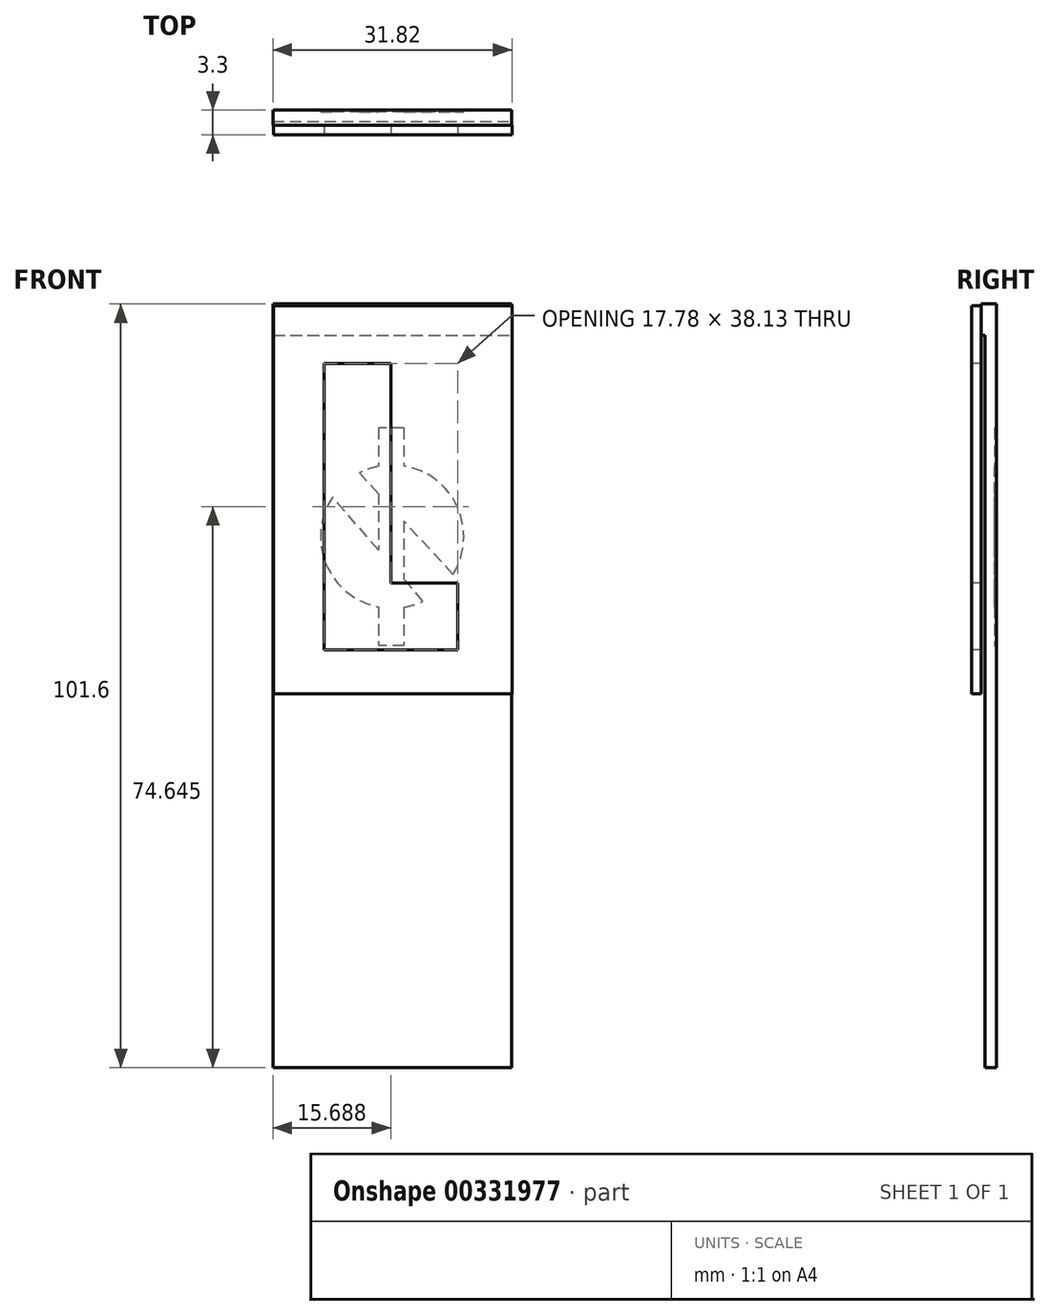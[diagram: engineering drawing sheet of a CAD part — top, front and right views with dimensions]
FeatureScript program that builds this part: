
annotation { "Feature Type Name" : "Feature", "Feature Type Description" : "" }
export const myFeature = defineFeature(function(context is Context, id is Id, definition is map)
    precondition{}
    {
        {
            var Q0;
            Q0=qCreatedBy(makeId("Front.planeOp"),FACE);
            var sketch = newSketch(context, id + "F0", { "sketchPlane" : qUnion([Q0])});
            skLineSegment(sketch, "E0.bottom", {"start": v(-28.9, 62.6) * mm, "end": v(2.85, 62.6) * mm});
            skLineSegment(sketch, "E0.top", {"start": v(-28.9, -39) * mm, "end": v(2.85, -39) * mm});
            skLineSegment(sketch, "E0.left", {"start": v(-28.9, 62.6) * mm, "end": v(-28.9, -39) * mm});
            skLineSegment(sketch, "E0.right", {"start": v(2.85, 62.6) * mm, "end": v(2.85, -39) * mm});
            skSolve(sketch);
        }
        {
            var Q0;
            Q0=makeQuery(id+"F0.imprint","IMPRINT",FACE,{"disambiguationData":[TD([[makeQuery(id+"F0.imprint","IMPRINT",EDGE,{"derivedFrom":sQuery(id+"F0.wireOp",EDGE,"E0.bottom")}),-1.0]])]});
            extrude(context, id + "F1", {"entities" : qUnion([Q0]), "depth" : 1.52 * mm});
        }
        {
            var Q0;
            Q0=makeQuery(id+"F1.opExtrude","CAP_FACE",FACE,{"disambiguationData":[OSD([sQuery(id+"F0.wireOp",EDGE,"E0.bottom"),sQuery(id+"F0.wireOp",EDGE,"E0.top"),sQuery(id+"F0.wireOp",EDGE,"E0.left"),sQuery(id+"F0.wireOp",EDGE,"E0.right")])],"isStart":false});
            var sketch = newSketch(context, id + "F2", { "sketchPlane" : qUnion([Q0])});
            skLineSegment(sketch, "E1.bottom", {"start": v(-28.9, 62.6) * mm, "end": v(2.85, 62.6) * mm});
            skLineSegment(sketch, "E1.top", {"start": v(-28.9, 58.42) * mm, "end": v(2.85, 58.42) * mm});
            skLineSegment(sketch, "E1.left", {"start": v(-28.9, 62.6) * mm, "end": v(-28.9, 58.42) * mm});
            skLineSegment(sketch, "E1.right", {"start": v(2.85, 62.6) * mm, "end": v(2.85, 58.42) * mm});
            skSolve(sketch);
        }
        {
            var Q0;
            Q0=makeQuery(id+"F2.imprint","IMPRINT",FACE,{"disambiguationData":[TD([[makeQuery(id+"F2.imprint","IMPRINT",EDGE,{"derivedFrom":sQuery(id+"F2.wireOp",EDGE,"E1.bottom")}),-1.0]])]});
            extrude(context, id + "F3", {"entities" : qUnion([Q0]), "operationType" : NewBodyOperationType.ADD, "depth" : 0.5 * mm});
        }
        {
            var Q0;
            Q0=makeQuery(id+"F3.opExtrude","CAP_FACE",FACE,{"disambiguationData":[OSD([sQuery(id+"F2.wireOp",EDGE,"E1.bottom"),sQuery(id+"F2.wireOp",EDGE,"E1.top"),sQuery(id+"F2.wireOp",EDGE,"E1.left"),sQuery(id+"F2.wireOp",EDGE,"E1.right")])],"isStart":false});
            cPlane(context, id + "F4", {"entities" : qUnion([Q0]), "cplaneType" : CPlaneType.OFFSET, "offset" : 0 * mm, "width" : 152.4 * mm, "height" : 152.4 * mm});
        }
        {
            var Q0;
            Q0=qCreatedBy(id+"F4.planeOp",FACE);
            var sketch = newSketch(context, id + "F5", { "sketchPlane" : qUnion([Q0])});
            skLineSegment(sketch, "E2.bottom", {"start": v(-28.83, 62.35) * mm, "end": v(2.92, 62.35) * mm});
            skLineSegment(sketch, "E2.top", {"start": v(-28.83, 10.75) * mm, "end": v(2.92, 10.75) * mm});
            skLineSegment(sketch, "E2.left", {"start": v(-28.83, 62.35) * mm, "end": v(-28.83, 10.75) * mm});
            skLineSegment(sketch, "E2.right", {"start": v(2.92, 62.35) * mm, "end": v(2.92, 10.75) * mm});
            skSolve(sketch);
        }
        {
            var Q0;
            Q0=makeQuery(id+"F5.imprint","IMPRINT",FACE,{"disambiguationData":[TD([[makeQuery(id+"F5.imprint","IMPRINT",EDGE,{"derivedFrom":sQuery(id+"F5.wireOp",EDGE,"E2.bottom")}),-1.0]])]});
            extrude(context, id + "F6", {"entities" : qUnion([Q0]), "operationType" : NewBodyOperationType.ADD, "depth" : 1.27 * mm});
        }
        {
            var Q0;
            Q0=makeQuery(id+"F6.opExtrude","CAP_FACE",FACE,{"disambiguationData":[OSD([sQuery(id+"F5.wireOp",EDGE,"E2.bottom"),sQuery(id+"F5.wireOp",EDGE,"E2.top"),sQuery(id+"F5.wireOp",EDGE,"E2.left"),sQuery(id+"F5.wireOp",EDGE,"E2.right")])],"isStart":false});
            var sketch = newSketch(context, id + "F7", { "sketchPlane" : qUnion([Q0])});
            skPoint(sketch, "E3.3.internal.snap0", {"position": v(-12.95, 62.35) * mm});
            skLineSegment(sketch, "E4", {"start": v(-22.1, 54.71) * mm, "end": v(-22.1, 16.58) * mm});
            skLineSegment(sketch, "E5", {"start": v(-22.1, 16.58) * mm, "end": v(-4.32, 16.58) * mm});
            skLineSegment(sketch, "E6", {"start": v(-4.32, 16.58) * mm, "end": v(-4.32, 25.47) * mm});
            skLineSegment(sketch, "E7", {"start": v(-4.32, 25.47) * mm, "end": v(-13.21, 25.47) * mm});
            skPoint(sketch, "E7.endSnap0", {"position": v(-13.21, 16.58) * mm});
            skLineSegment(sketch, "E8", {"start": v(-13.21, 25.47) * mm, "end": v(-13.21, 54.71) * mm});
            skLineSegment(sketch, "E9", {"start": v(-22.1, 54.71) * mm, "end": v(-13.21, 54.71) * mm});
            skSolve(sketch);
        }
        {
            var Q0;
            Q0=makeQuery(id+"F7.imprint","IMPRINT",FACE,{"disambiguationData":[TD([[makeQuery(id+"F7.imprint","IMPRINT",EDGE,{"derivedFrom":sQuery(id+"F7.wireOp",EDGE,"E4")}),1.0]])]});
            extrude(context, id + "F8", {"entities" : qUnion([Q0]), "operationType" : NewBodyOperationType.REMOVE, "oppositeDirection" : true, "depth" : 1.27 * mm});
        }
        {
            var Q0;
            Q0=makeQuery(id+"F1.opExtrude","CAP_FACE",FACE,{"disambiguationData":[OSD([sQuery(id+"F0.wireOp",EDGE,"E0.bottom"),sQuery(id+"F0.wireOp",EDGE,"E0.top"),sQuery(id+"F0.wireOp",EDGE,"E0.left"),sQuery(id+"F0.wireOp",EDGE,"E0.right")])],"isStart":true});
            var sketch = newSketch(context, id + "F9", { "sketchPlane" : qUnion([Q0])});
            skCircle(sketch, "E10", {"center": v(13.03, 31.66) * mm, "radius": 12.7 * mm});
            skPoint(sketch, "E10.centerSnap0", {"position": v(13.03, 62.6) * mm});
            skCircle(sketch, "E11", {"center": v(13.03, 31.66) * mm, "radius": 9.53 * mm});
            skLineSegment(sketch, "E12", {"start": v(4.94, 26.64) * mm, "end": v(17.4, 40.13) * mm});
            skLineSegment(sketch, "E13", {"start": v(8.92, 23.06) * mm, "end": v(20.97, 36.92) * mm});
            skSolve(sketch);
        }
        {
            var Q0;
            {var subQ0=sQuery(id+"F9.wireOp",EDGE,"E12");Q0=makeQuery(id+"F9.imprint","IMPRINT",FACE,{"disambiguationData":[TD([[makeQuery(id+"F9.imprint","IMPRINT",EDGE,{"derivedFrom":subQ0}),1.0]])]});}
            var Q1;
            {var subQ0=sQuery(id+"F9.wireOp",EDGE,"E13");Q1=makeQuery(id+"F9.imprint","IMPRINT",FACE,{"disambiguationData":[TD([[makeQuery(id+"F9.imprint","IMPRINT",EDGE,{"derivedFrom":subQ0}),-1.0]])]});}
            extrude(context, id + "F10", {"entities" : qUnion([Q0, Q1]), "operationType" : NewBodyOperationType.REMOVE, "depth" : -0.25 * mm});
        }
        {
            var Q0;
            Q0=makeQuery(id+"F1.opExtrude","CAP_FACE",FACE,{"disambiguationData":[OSD([sQuery(id+"F0.wireOp",EDGE,"E0.bottom"),sQuery(id+"F0.wireOp",EDGE,"E0.top"),sQuery(id+"F0.wireOp",EDGE,"E0.left"),sQuery(id+"F0.wireOp",EDGE,"E0.right")])],"isStart":true});
            var sketch = newSketch(context, id + "F11", { "sketchPlane" : qUnion([Q0])});
            skLineSegment(sketch, "E14.bottom", {"start": v(11.46, 46.09) * mm, "end": v(14.85, 46.09) * mm});
            skLineSegment(sketch, "E14.top", {"start": v(11.46, 17.18) * mm, "end": v(14.85, 17.18) * mm});
            skLineSegment(sketch, "E14.left", {"start": v(11.46, 46.09) * mm, "end": v(11.46, 17.18) * mm});
            skLineSegment(sketch, "E14.right", {"start": v(14.85, 46.09) * mm, "end": v(14.85, 17.18) * mm});
            skPoint(sketch, "E15", {"position": v(14.85, 41) * mm});
            skPoint(sketch, "E16", {"position": v(11.46, 22.26) * mm});
            skSolve(sketch);
        }
        {
            var Q0;
            {var subQ0=sQuery(id+"F11.wireOp",EDGE,"E14.bottom");Q0=makeQuery(id+"F11.imprint","IMPRINT",FACE,{"disambiguationData":[TD([[makeQuery(id+"F11.imprint","IMPRINT",EDGE,{"derivedFrom":subQ0}),-1.0]])]});}
            var Q1;
            {var subQ0=sQuery(id+"F11.wireOp",EDGE,"E14.left");var subQ1=makeQuery(id+"F10.boolean.opBoolean","COPY",EDGE,{"derivedFrom":makeQuery(id+"F10.opExtrude","CAP_EDGE",EDGE,{"disambiguationData":[OSD([sQuery(id+"F9.wireOp",EDGE,"E12")])],"isStart":true})});var subQ2=makeQuery(id+"F11.imprint","INTERSECT",VERTEX,{"derivedFrom":[subQ1,subQ0]});Q1=makeQuery(id+"F11.imprint","IMPRINT",FACE,{"disambiguationData":[TD([[makeQuery(id+"F11.imprint","IMPRINT",EDGE,{"disambiguationData":[TD([[subQ2,-1.0]])],"derivedFrom":subQ0}),1.0]])]});}
            var Q2;
            {var subQ0=sQuery(id+"F11.wireOp",EDGE,"E14.left");var subQ1=sQuery(id+"F9.wireOp",EDGE,"E12");var subQ5=makeQuery(id+"F10.boolean.opBoolean","COPY",EDGE,{"derivedFrom":makeQuery(id+"F10.opExtrude","CAP_EDGE",EDGE,{"disambiguationData":[OSD([subQ1])],"isStart":true})});var subQ6=makeQuery(id+"F11.imprint","INTERSECT",VERTEX,{"derivedFrom":[subQ5,subQ0]});Q2=makeQuery(id+"F11.imprint","IMPRINT",FACE,{"disambiguationData":[TD([[makeQuery(id+"F11.imprint","IMPRINT",EDGE,{"disambiguationData":[TD([[subQ6,-1.0]])],"derivedFrom":subQ5}),1.0]])]});}
            var Q3;
            {var subQ0=sQuery(id+"F11.wireOp",EDGE,"E14.left");var subQ1=sQuery(id+"F9.wireOp",EDGE,"E13");var subQ2=makeQuery(id+"F10.boolean.opBoolean","COPY",EDGE,{"derivedFrom":makeQuery(id+"F10.opExtrude","CAP_EDGE",EDGE,{"disambiguationData":[OSD([subQ1])],"isStart":true})});var subQ3=makeQuery(id+"F11.imprint","INTERSECT",VERTEX,{"derivedFrom":[subQ2,subQ0]});Q3=makeQuery(id+"F11.imprint","IMPRINT",FACE,{"disambiguationData":[TD([[makeQuery(id+"F11.imprint","IMPRINT",EDGE,{"disambiguationData":[TD([[subQ3,-1.0]])],"derivedFrom":subQ2}),-1.0]])]});}
            var Q4;
            {var subQ0=sQuery(id+"F11.wireOp",EDGE,"E14.top");Q4=makeQuery(id+"F11.imprint","IMPRINT",FACE,{"disambiguationData":[TD([[makeQuery(id+"F11.imprint","IMPRINT",EDGE,{"derivedFrom":subQ0}),1.0]])]});}
            extrude(context, id + "F12", {"entities" : qUnion([Q0, Q1, Q2, Q3, Q4]), "operationType" : NewBodyOperationType.REMOVE, "oppositeDirection" : true, "depth" : 0.25 * mm});
        }
    });
